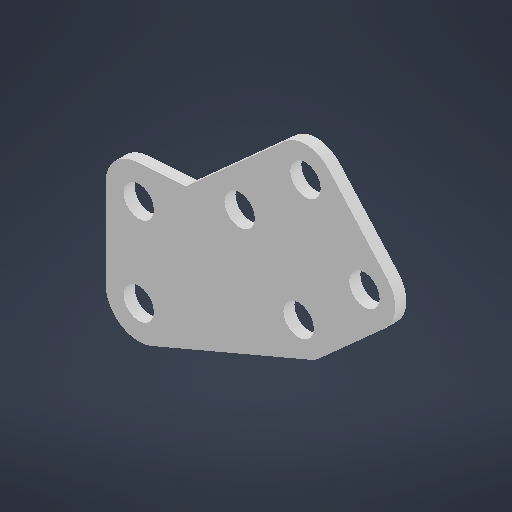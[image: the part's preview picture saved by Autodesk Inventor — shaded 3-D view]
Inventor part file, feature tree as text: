
AUTODESK INVENTOR PART (.ipt)
format: ipt  version: 2025.2 (Build 292293000, 293)  size: 225,280 bytes
history: native  units: in
note: dims shown in document units (in); Inventor stores cm internally (conversion verified against a paired STEP export)
features: extrude x1, sketch x1
ambient origin geometry x8: Origin, YZ Plane, XZ Plane, XY Plane, X Axis, Y Axis, Z Axis, Center Point
bodies: Solid1 (feature_tree)
feature tree (2):
  extrude  "Extrusion1"  Depth=0.0625in
  sketch  "Sketch1"  dims[d0=0.35in d1=0.35in d2=0.35in d3=0.375in d4=0.375in d5=0.35in d9=0.25in d10=0.0625in d11=0.0in]
